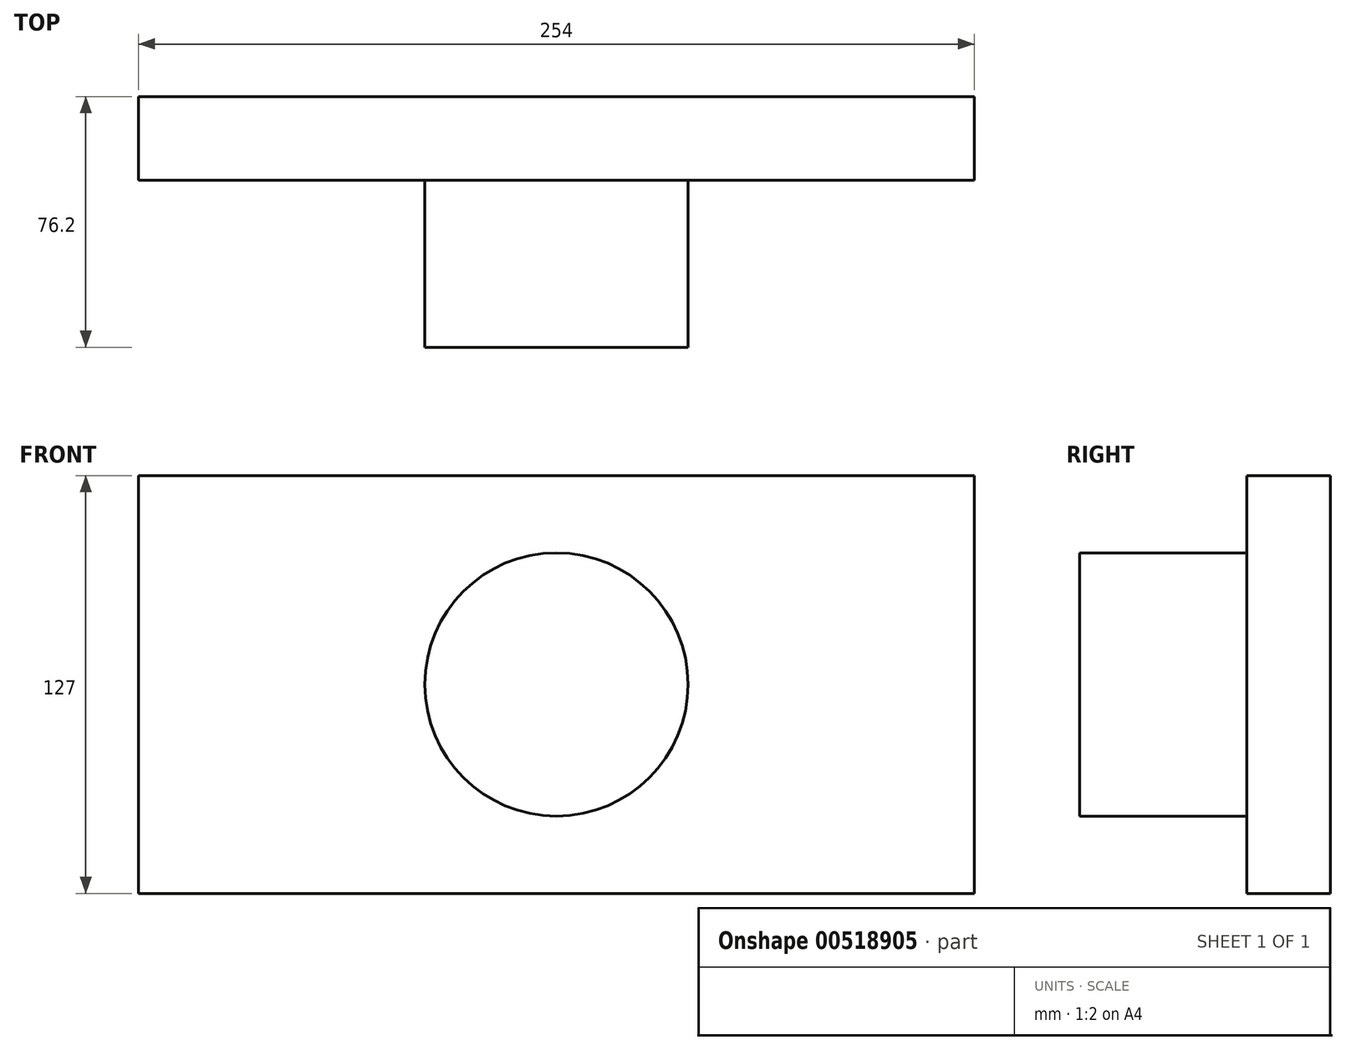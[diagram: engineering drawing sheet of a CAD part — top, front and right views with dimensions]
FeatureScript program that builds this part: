
annotation { "Feature Type Name" : "Feature", "Feature Type Description" : "" }
export const myFeature = defineFeature(function(context is Context, id is Id, definition is map)
    precondition{}
    {
        {
            var Q0;
            Q0=qCreatedBy(makeId("Front.planeOp"),FACE);
            var sketch = newSketch(context, id + "F0", { "sketchPlane" : qUnion([Q0])});
            skLineSegment(sketch, "E0.bottom", {"start": v(-127, 63.5) * mm, "end": v(127, 63.5) * mm});
            skLineSegment(sketch, "E0.top", {"start": v(-127, -63.5) * mm, "end": v(127, -63.5) * mm});
            skLineSegment(sketch, "E0.left", {"start": v(-127, 63.5) * mm, "end": v(-127, -63.5) * mm});
            skLineSegment(sketch, "E0.right", {"start": v(127, 63.5) * mm, "end": v(127, -63.5) * mm});
            skPoint(sketch, "E0.middle", {"position": v(0, 0) * mm});
            skSolve(sketch);
        }
        {
            var Q0;
            Q0 = qSketchRegion(id + "F0", true);
            extrude(context, id + "F1", {"entities" : qUnion([Q0]), "depth" : 25.4 * mm, "offsetDistance" : 25.4 * mm});
        }
        {
            var Q0;
            Q0=makeQuery(id+"F1.opExtrude","CAP_FACE",FACE,{"disambiguationData":[OSD([sQuery(id+"F0.wireOp",EDGE,"E0.bottom"),sQuery(id+"F0.wireOp",EDGE,"E0.top"),sQuery(id+"F0.wireOp",EDGE,"E0.left"),sQuery(id+"F0.wireOp",EDGE,"E0.right")])],"isStart":false});
            var sketch = newSketch(context, id + "F2", { "sketchPlane" : qUnion([Q0])});
            skCircle(sketch, "E1", {"center": v(0, 0) * mm, "radius": 40 * mm});
            skSolve(sketch);
        }
        {
            var Q0;
            Q0=makeQuery(id+"F2.imprint","IMPRINT",FACE,{"disambiguationData":[TD([[makeQuery(id+"F2.imprint","IMPRINT",EDGE,{"derivedFrom":sQuery(id+"F2.wireOp",EDGE,"E1")}),1.0]])]});
            extrude(context, id + "F3", {"entities" : qUnion([Q0]), "operationType" : NewBodyOperationType.ADD, "depth" : 50.8 * mm, "offsetDistance" : 25.4 * mm});
        }
    });
